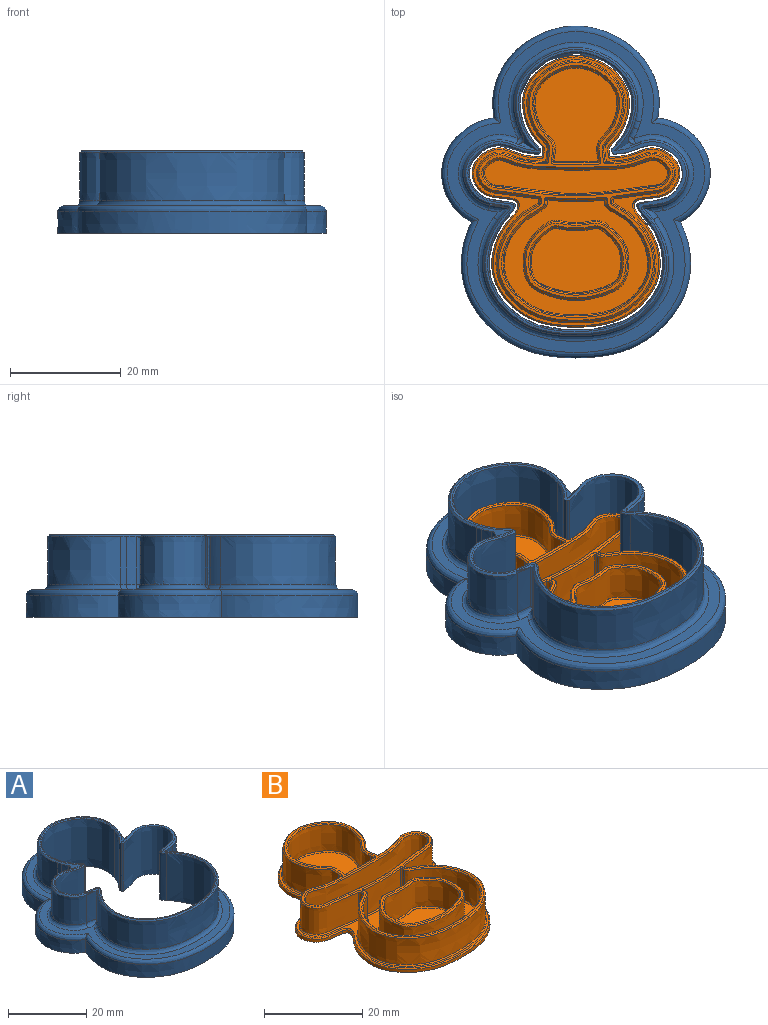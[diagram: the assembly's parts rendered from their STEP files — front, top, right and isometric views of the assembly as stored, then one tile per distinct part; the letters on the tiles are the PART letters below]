
ASSEMBLY  parts=2 mates=1
PART A: 78 faces, bbox 49x60.4x15.4 mm
  f0: extruded ~8.65x1.72mm, area 16.4mm2, adj f1,f49,f71,f73
  f1: extruded ~8.65x1.07mm, area 9.7mm2, adj f0,f2,f51,f70
  f2: extruded ~22.3x13.21mm, area 341.1mm2, adj f1,f3,f53,f69
  f3: extruded ~8.65x1.24mm, area 11.3mm2, adj f2,f4,f55,f68
  f4: extruded ~8.65x1.55mm, area 14.9mm2, adj f3,f57,f65,f67
  f5: extruded ~11.82x10.64mm, area 180.7mm2, adj f6,f54,f56,f58,f65
  f6: extruded ~8.65x3.1mm, area 27mm2, adj f5,f12,f52,f59
  f7: extruded ~8.65x1.79mm, area 20.3mm2, adj f8,f12,f48,f60
  f8: extruded ~33.47x20.95mm, area 554.9mm2, adj f7,f9,f46,f61
  f9: extruded ~8.65x1.91mm, area 21.7mm2, adj f8,f13,f44,f62
  f10: extruded ~8.65x3.11mm, area 27.2mm2, adj f11,f13,f43,f64
  f11: extruded ~11.79x11.05mm, area 180.7mm2, adj f10,f45,f47,f63,f73
  f12: extruded ~9.02x0.46mm, area 6.2mm2, adj f6,f7,f50,f59,f60
  f13: extruded ~9.05x0.45mm, area 6.1mm2, adj f9,f10,f42,f62,f64
  f14: extruded ~20.32x14.75mm, area 548mm2, adj f15,f23,f25,f40
  f15: extruded ~14.75x4.59mm, area 81.3mm2, adj f14,f16,f25,f39
  f16: extruded ~14.75x0.75mm, area 11.4mm2, adj f15,f25,f31,f38
  f17: extruded ~14.75x12.34mm, area 378.5mm2, adj f18,f25,f31,f36
  f18: extruded ~14.75x2.07mm, area 40mm2, adj f17,f19,f25,f35
  f19: extruded ~31.46x21.05mm, area 949.2mm2, adj f18,f20,f25,f34
  f20: extruded ~14.75x2.09mm, area 40.3mm2, adj f19,f21,f25,f33
  f21: extruded ~15x12.32mm, area 384.3mm2, adj f20,f24,f25,f32,f33
  f22: extruded ~15x1.45mm, area 10.9mm2, adj f23,f24,f25,f32,f41
  f23: extruded ~14.75x4.63mm, area 82mm2, adj f14,f22,f25,f41
  f24: plane 51.83x40.4mm, normal (0,0,1), area 75.5mm2, adj f21,f22,f32,f33,f34,f35,f36,f37
  f25: plane 60.06x48.59mm, normal (0,0,-1), area 864.1mm2, adj f14,f15,f16,f17,f18,f19,f20,f21
  f26: extruded ~18.8x9.47mm, area 103.5mm2, adj f25,f27,f29,f77
  f27: extruded ~41.47x24.6mm, area 303mm2, adj f25,f26,f28,f76
  f28: extruded ~18.8x9.47mm, area 103.5mm2, adj f25,f27,f29,f74
  f29: extruded ~30.08x16.65mm, area 203.3mm2, adj f25,f26,f28,f75
  f30: plane 58.05x46.61mm, normal (0,0,1), area 339.4mm2, adj f58,f59,f60,f61,f62,f63,f64,f67
  f31: cylinder r=0.4mm len=14.75mm, axis (0,0,-1), area 8.9mm2, adj f16,f17,f25,f37
  f32: cylinder r=0.4mm len=15mm, axis (0,0,-1), area 9.2mm2, adj f21,f22,f24,f25
  f33: bspline ~2.76x2.76mm, area 1.2mm2, adj f20,f21,f24,f34
  f34: bspline ~31.98x22.73mm, area 23mm2, adj f19,f24,f33,f35
  f35: bspline ~2.17x1.01mm, area 0.9mm2, adj f18,f24,f34,f36
  f36: bspline ~12.65x11.02mm, area 9.2mm2, adj f17,f24,f35,f37
  f37: cone r=0.15mm half-angle=45deg, axis (0,0,-1), area 0.1mm2, adj f24,f31,f36,f38
  f38: bspline ~0.77x0.33mm, area 0.2mm2, adj f16,f24,f37,f39
  f39: bspline ~4.75x3.2mm, area 2mm2, adj f15,f24,f38,f40
  f40: bspline ~20.99x12.96mm, area 13.3mm2, adj f14,f24,f39,f41
  f41: bspline ~5x3.4mm, area 1.8mm2, adj f22,f23,f24,f40
  f42: bspline ~1.11x0.73mm, area 0.5mm2, adj f13,f24,f43,f44
  f43: bspline ~3.18x0.77mm, area 1.6mm2, adj f10,f24,f42,f45
  f44: bspline ~2.21x1.96mm, area 1.2mm2, adj f9,f24,f42,f46
  f45: bspline ~11.82x11.13mm, area 10.9mm2, adj f11,f24,f43,f47
  f46: bspline ~33.51x20.95mm, area 31.4mm2, adj f8,f24,f44,f48
  f47: bspline ~4.3x1.78mm, area 2.3mm2, adj f11,f24,f45,f49,f73
  f48: bspline ~2.09x1.87mm, area 1.2mm2, adj f7,f24,f46,f50
  f49: bspline ~5.43x4.18mm, area 3.9mm2, adj f0,f24,f47,f51,f73
  f50: bspline ~1.04x0.63mm, area 0.5mm2, adj f12,f24,f48,f52
  f51: bspline ~1.16x0.67mm, area 0.5mm2, adj f1,f24,f49,f53
  f52: bspline ~3.17x0.76mm, area 1.5mm2, adj f6,f24,f50,f54
  f53: bspline ~22.39x13.21mm, area 19.2mm2, adj f2,f24,f51,f55
  f54: bspline ~11.9x10.68mm, area 10.7mm2, adj f5,f24,f52,f56
  f55: bspline ~1.33x0.73mm, area 0.6mm2, adj f3,f24,f53,f57
  f56: bspline ~4.26x1.86mm, area 2.5mm2, adj f5,f24,f54,f57,f65
  f57: bspline ~5.25x4.1mm, area 3.8mm2, adj f4,f24,f55,f56,f65
  f58: bspline ~15.03x11.21mm, area 34.8mm2, adj f5,f30,f59,f66
  f59: bspline ~4x1.52mm, area 4.2mm2, adj f6,f12,f30,f58,f60
  f60: bspline ~4.13x3.86mm, area 3.3mm2, adj f7,f12,f30,f59,f61
  f61: bspline ~35.49x33.1mm, area 103.4mm2, adj f8,f30,f60,f62
  f62: bspline ~4.37x4.06mm, area 3.5mm2, adj f9,f13,f30,f61,f64
  f63: bspline ~15.05x11.13mm, area 34.6mm2, adj f11,f30,f64,f72
  f64: bspline ~4.68x1.69mm, area 4.3mm2, adj f10,f13,f30,f62,f63
  f65: cylinder r=1mm len=8.65mm, axis (0,0,-1), area 20.4mm2, adj f4,f5,f56,f57,f66
  f66: sphere r=1mm, area 1.7mm2, adj f58,f65,f67
  f67: bspline ~3.69x2.44mm, area 2.8mm2, adj f4,f30,f66,f68
  f68: bspline ~2.04x1.52mm, area 2.1mm2, adj f3,f30,f67,f69
  f69: bspline ~24.34x23.94mm, area 64.1mm2, adj f2,f30,f68,f70
  f70: bspline ~1.8x1.43mm, area 1.8mm2, adj f1,f30,f69,f71
  f71: bspline ~3.93x2.53mm, area 3.1mm2, adj f0,f30,f70,f72
  f72: sphere r=1mm, area 2.5mm2, adj f63,f71,f73
  f73: cylinder r=1mm len=8.65mm, axis (0,0,-1), area 20.3mm2, adj f0,f11,f47,f49,f72
  f74: bspline ~20.41x15.79mm, area 40.8mm2, adj f28,f30,f75,f76
  f75: bspline ~30.15x18.21mm, area 79.5mm2, adj f29,f30,f74,f77
  f76: bspline ~41.49x26.16mm, area 118mm2, adj f27,f30,f74,f77
  f77: bspline ~20.41x15.79mm, area 40.8mm2, adj f26,f30,f75,f76
PART B: 117 faces, bbox 38x49.5x8.3 mm
  f0: plane 26.25x21.02mm, normal (0,0,1), area 192mm2, adj f108,f109,f111,f112,f113,f115,f116
  f1: extruded ~12.43x9.33mm, area 18.6mm2, adj f6,f8,f45,f100
  f2: extruded ~19.32x18.13mm, area 37.6mm2, adj f8,f45,f46,f97
  f3: extruded ~12.43x9.33mm, area 18.6mm2, adj f4,f8,f46,f93
  f4: extruded ~2.9x1.14mm, area 2.8mm2, adj f3,f5,f8,f94
  f5: extruded ~30.46x20.21mm, area 46.5mm2, adj f4,f6,f8,f96
  f6: extruded ~2.91x1.14mm, area 2.8mm2, adj f1,f5,f8,f98
  f7: plane 48.94x37.46mm, normal (0,0,1), area 98.6mm2, adj f79,f80,f81,f82,f84,f85,f86,f87
  f8: plane 49.16x37.6mm, normal (0,0,-1), area 1164.8mm2, adj f1,f2,f3,f4,f5,f6,f45,f46
  f9: extruded ~10.45x6.5mm, area 68mm2, adj f43,f44,f54,f112
  f10: extruded ~6.5x0.57mm, area 3.7mm2, adj f11,f43,f57,f108
  f11: extruded ~6.5x0.09mm, area 0.6mm2, adj f10,f12,f55,f109
  f12: extruded ~26.47x20.26mm, area 417mm2, adj f11,f13,f53,f111
  f13: extruded ~6.5x0.12mm, area 0.8mm2, adj f12,f31,f51,f113
  f14: extruded ~6.5x0.72mm, area 4.7mm2, adj f15,f39,f73,f106
  f15: extruded ~16.41x15.32mm, area 285mm2, adj f14,f16,f75,f104
  f16: extruded ~6.5x0.72mm, area 4.7mm2, adj f15,f41,f77,f102
  f17: extruded ~17.39x17.32mm, area 306.7mm2, adj f18,f30,f66,f87
  f18: extruded ~6.5x0.78mm, area 5.1mm2, adj f17,f40,f64,f89
  f19: extruded ~6.5x0.78mm, area 5.1mm2, adj f20,f40,f60,f92
  f20: extruded ~11.51x8.03mm, area 173.6mm2, adj f19,f21,f58,f90
  f21: extruded ~6.5x1.02mm, area 7.1mm2, adj f20,f22,f59,f88
  f22: extruded ~6.5x0.19mm, area 1.7mm2, adj f21,f23,f61,f86
  f23: extruded ~28.38x21.26mm, area 435.1mm2, adj f22,f24,f63,f84
  f24: extruded ~6.5x0.14mm, area 1.3mm2, adj f23,f25,f65,f82
  f25: extruded ~6.5x1.03mm, area 7.3mm2, adj f24,f26,f67,f80
  f26: extruded ~11.51x8.02mm, area 173.3mm2, adj f25,f27,f69,f79
  f27: extruded ~6.5x0.78mm, area 5.1mm2, adj f26,f42,f71,f81
  f28: extruded ~33.4x6.5mm, area 485.6mm2, adj f78,f107
  f29: extruded ~7.98x6.5mm, area 51.9mm2, adj f39,f41,f74,f103
  f30: extruded ~6.5x0.78mm, area 5.1mm2, adj f17,f42,f68,f85
  f31: extruded ~6.5x0.54mm, area 3.6mm2, adj f13,f44,f50,f115
  f32: plane 47.02x35.51mm, normal (0,0,1), area 100.3mm2, adj f50,f51,f52,f53,f54,f55,f56,f57
  f33: plane 17.37x15.23mm, normal (0,0,1), area 187.2mm2, adj f102,f103,f104,f106
  f34: plane 33.13x6.06mm, normal (0,0,1), area 120.3mm2, adj f107
  f35: extruded ~16.63x12.04mm, area 305.5mm2, adj f47,f48
  f36: extruded ~18.63x14.04mm, area 347.3mm2, adj f49,f116
  f37: plane 18.29x13.69mm, normal (0,0,1), area 25.9mm2, adj f48,f49
  f38: plane 16.31x11.71mm, normal (0,0,1), area 154.5mm2, adj f47
  f39: cylinder r=0.25mm len=6.5mm, axis (0,0,-1), area 2.8mm2, adj f14,f29,f72,f105
  f40: cylinder r=0.25mm len=6.5mm, axis (0,0,-1), area 2.4mm2, adj f18,f19,f62,f91
  f41: cylinder r=0.25mm len=6.5mm, axis (0,0,-1), area 2.8mm2, adj f16,f29,f76,f101
  f42: cylinder r=0.25mm len=6.5mm, axis (0,0,-1), area 2.4mm2, adj f27,f30,f70,f83
  f43: cylinder r=0.25mm len=6.5mm, axis (0,0,-1), area 3.2mm2, adj f9,f10,f56,f110
  f44: cylinder r=0.25mm len=6.5mm, axis (0,0,-1), area 3.2mm2, adj f9,f31,f52,f114
  f45: cylinder r=0.25mm len=0.75mm, axis (0,0,-1), area 0.3mm2, adj f1,f2,f8,f99
  f46: cylinder r=0.25mm len=0.75mm, axis (0,0,-1), area 0.3mm2, adj f2,f3,f8,f95
  f47: bspline ~16.61x12.03mm, area 16.4mm2, adj f35,f38
  f48: bspline ~17.15x12.55mm, area 17mm2, adj f35,f37
  f49: bspline ~18.61x13.99mm, area 18.6mm2, adj f36,f37
  f50: bspline ~0.54x0.32mm, area 0.2mm2, adj f31,f32,f51,f52
  f51: bspline ~0.27x0.25mm, area 0mm2, adj f13,f32,f50,f53
  f52: cone r=0.5mm half-angle=45deg, axis (0,0,1), area 0.3mm2, adj f32,f44,f50,f54
  f53: bspline ~27.16x20.57mm, area 22.9mm2, adj f12,f32,f51,f55
  f54: bspline ~10.45x0.53mm, area 3.7mm2, adj f9,f32,f52,f56
  f55: bspline ~0.26x0.25mm, area 0mm2, adj f11,f32,f53,f57
  f56: cone r=0.5mm half-angle=45deg, axis (0,0,1), area 0.3mm2, adj f32,f43,f54,f57
  f57: bspline ~0.57x0.32mm, area 0.2mm2, adj f10,f32,f55,f56
  f58: bspline ~12.65x8.23mm, area 9.3mm2, adj f20,f32,f59,f60
  f59: bspline ~1.47x0.58mm, area 0.5mm2, adj f21,f32,f58,f61
  f60: bspline ~0.79x0.28mm, area 0.3mm2, adj f19,f32,f58,f62
  f61: bspline ~0.41x0.4mm, area 0.1mm2, adj f22,f32,f59,f63
  f62: cone r=0.5mm half-angle=45deg, axis (0,0,1), area 0.2mm2, adj f32,f40,f60,f64
  f63: bspline ~28.54x22.31mm, area 23.5mm2, adj f23,f32,f61,f65
  f64: bspline ~0.81x0.36mm, area 0.3mm2, adj f18,f32,f62,f66
  f65: bspline ~0.33x0.33mm, area 0.1mm2, adj f24,f32,f63,f67
  f66: bspline ~17.46x17.43mm, area 16.5mm2, adj f17,f32,f64,f68
  f67: bspline ~1.49x0.67mm, area 0.5mm2, adj f25,f32,f65,f69
  f68: bspline ~0.81x0.36mm, area 0.3mm2, adj f30,f32,f66,f70
  f69: bspline ~12.6x8.22mm, area 9.3mm2, adj f26,f32,f67,f71
  f70: cone r=0.5mm half-angle=45deg, axis (0,0,1), area 0.2mm2, adj f32,f42,f68,f71
  f71: bspline ~0.79x0.28mm, area 0.3mm2, adj f27,f32,f69,f70
  f72: cone r=0.5mm half-angle=45deg, axis (0,0,1), area 0.2mm2, adj f32,f39,f73,f74
  f73: bspline ~0.75x0.36mm, area 0.3mm2, adj f14,f32,f72,f75
  f74: bspline ~7.99x0.36mm, area 2.8mm2, adj f29,f32,f72,f76
  f75: bspline ~16.66x15.87mm, area 15.7mm2, adj f15,f32,f73,f77
  f76: cone r=0.5mm half-angle=45deg, axis (0,0,1), area 0.2mm2, adj f32,f41,f74,f77
  f77: bspline ~0.75x0.36mm, area 0.3mm2, adj f16,f32,f75,f76
  f78: bspline ~34.16x7.08mm, area 26mm2, adj f28,f32
  f79: bspline ~12.75x8.75mm, area 9.5mm2, adj f7,f26,f80,f81
  f80: bspline ~1.06x0.51mm, area 0.3mm2, adj f7,f25,f79,f82
  f81: bspline ~0.79x0.28mm, area 0.3mm2, adj f7,f27,f79,f83
  f82: bspline ~0.31x0.3mm, area 0.1mm2, adj f7,f24,f80,f84
  f83: cone r=0.25mm half-angle=45deg, axis (0,0,1), area 0.1mm2, adj f42,f81,f85
  f84: bspline ~29.04x22.79mm, area 23.9mm2, adj f7,f23,f82,f86
  f85: bspline ~0.81x0.36mm, area 0.3mm2, adj f7,f30,f83,f87
  f86: bspline ~0.35x0.34mm, area 0.1mm2, adj f7,f22,f84,f88
  f87: bspline ~17.85x17.64mm, area 16.7mm2, adj f7,f17,f85,f89
  f88: bspline ~1.05x0.45mm, area 0.3mm2, adj f7,f21,f86,f90
  f89: bspline ~0.81x0.36mm, area 0.3mm2, adj f7,f18,f87,f91
  f90: bspline ~11.77x8.52mm, area 9.5mm2, adj f7,f20,f88,f92
  f91: cone r=0.25mm half-angle=45deg, axis (0,0,1), area 0.1mm2, adj f40,f89,f92
  f92: bspline ~0.79x0.28mm, area 0.3mm2, adj f7,f19,f90,f91
  f93: bspline ~12.48x9.51mm, area 8.6mm2, adj f3,f7,f94,f95
  f94: bspline ~3.32x1.4mm, area 1.4mm2, adj f4,f7,f93,f96
  f95: cone r=0.5mm half-angle=45deg, axis (0,0,1), area 0.2mm2, adj f7,f46,f93,f97
  f96: bspline ~30.48x21.38mm, area 21.8mm2, adj f5,f7,f94,f98
  f97: bspline ~19.39x18.17mm, area 17.4mm2, adj f2,f7,f95,f99
  f98: bspline ~3.32x1.4mm, area 1.4mm2, adj f6,f7,f96,f100
  f99: cone r=0.5mm half-angle=45deg, axis (0,0,1), area 0.2mm2, adj f7,f45,f97,f100
  f100: bspline ~12.48x9.51mm, area 8.6mm2, adj f1,f7,f98,f99
  f101: cone r=0.25mm half-angle=45deg, axis (0,0,1), area 0.1mm2, adj f41,f102,f103
  f102: bspline ~0.75x0.36mm, area 0.3mm2, adj f16,f33,f101,f104
  f103: bspline ~7.98x0.36mm, area 2.8mm2, adj f29,f33,f101,f105
  f104: bspline ~16.45x15.36mm, area 15.4mm2, adj f15,f33,f102,f106
  f105: cone r=0.25mm half-angle=45deg, axis (0,0,1), area 0.1mm2, adj f39,f103,f106
  f106: bspline ~0.75x0.36mm, area 0.3mm2, adj f14,f33,f104,f105
  f107: bspline ~33.62x6.5mm, area 25.6mm2, adj f28,f34
  f108: bspline ~0.68x0.33mm, area 0.2mm2, adj f0,f10,f109,f110
  f109: bspline ~0.27x0.25mm, area 0mm2, adj f0,f11,f108,f111
  f110: cone r=0.25mm half-angle=45deg, axis (0,0,1), area 0.1mm2, adj f43,f108,f112
  f111: bspline ~26.67x20.26mm, area 22.5mm2, adj f0,f12,f109,f113
  f112: bspline ~10.5x0.53mm, area 3.7mm2, adj f0,f9,f110,f114
  f113: bspline ~0.27x0.25mm, area 0mm2, adj f0,f13,f111,f115
  f114: cone r=0.25mm half-angle=45deg, axis (0,0,1), area 0.1mm2, adj f44,f112,f115
  f115: bspline ~0.65x0.33mm, area 0.2mm2, adj f0,f31,f113,f114
  f116: bspline ~19.15x14.56mm, area 19.2mm2, adj f0,f36
PLACE A t=(-17.34,-5.22,-2.6)mm
PLACE B t=(-17.34,-5.16,-2.6)mm
MATE fastened B.f8 <-> A.f25  axis (0,0,-1) through (-17.34,-8.12,-2.6)mm
